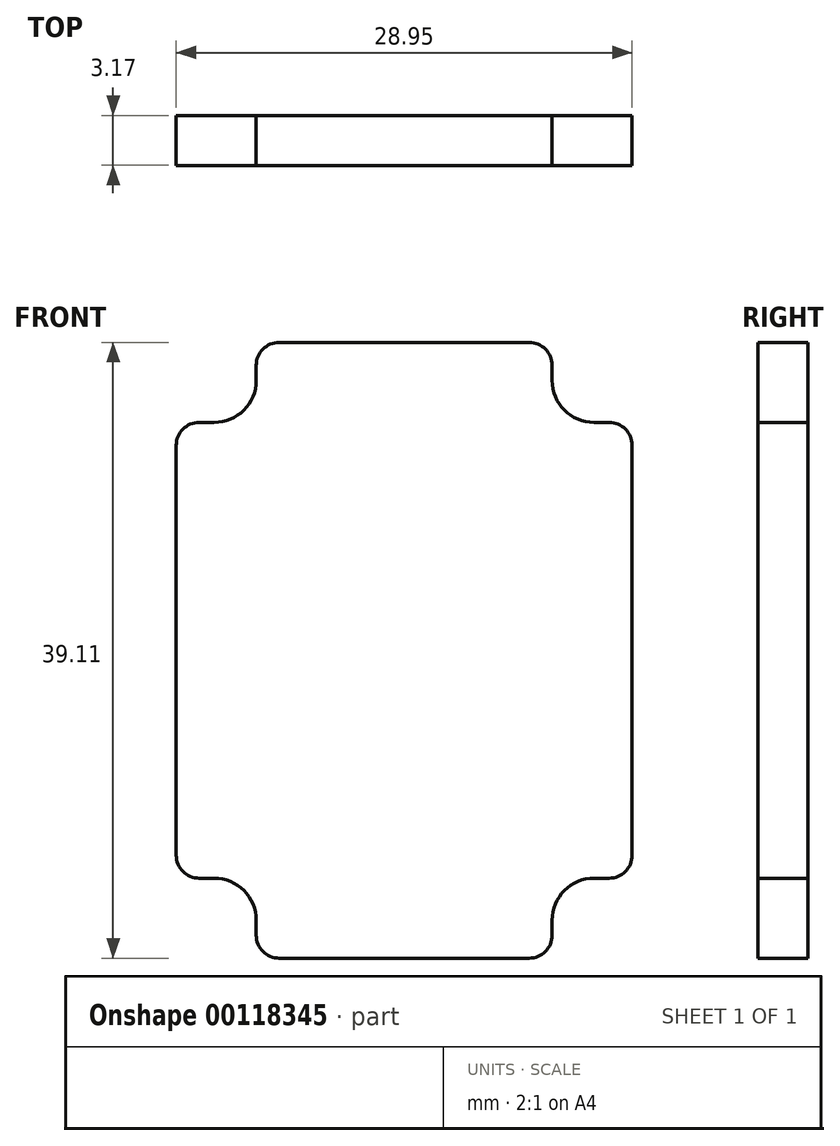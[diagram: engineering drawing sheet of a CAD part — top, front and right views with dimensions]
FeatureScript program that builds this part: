
annotation { "Feature Type Name" : "Feature", "Feature Type Description" : "" }
export const myFeature = defineFeature(function(context is Context, id is Id, definition is map)
    precondition{}
    {
        {
            var Q0;
            Q0=qCreatedBy(makeId("Front.planeOp"),FACE);
            var sketch = newSketch(context, id + "F0", { "sketchPlane" : qUnion([Q0])});
            skArc(sketch, "E0.0", {"start": v(-12.72, 14.33) * mm, "mid": v(-13.75, 13.9) * mm, "end": v(-14.18, 12.87) * mm});
            skLineSegment(sketch, "E0.1", {"start": v(12.36, -14.62) * mm, "end": v(13.31, -14.62) * mm});
            skArc(sketch, "E0.2", {"start": v(12.36, -14.62) * mm, "mid": v(10.47, -15.4) * mm, "end": v(9.7, -17.3) * mm});
            skLineSegment(sketch, "E0.3", {"start": v(9.7, -17.3) * mm, "end": v(9.7, -18.24) * mm});
            skArc(sketch, "E0.4", {"start": v(8.23, -19.7) * mm, "mid": v(9.26, -19.28) * mm, "end": v(9.7, -18.24) * mm});
            skLineSegment(sketch, "E0.5", {"start": v(-7.64, -19.7) * mm, "end": v(8.23, -19.7) * mm});
            skArc(sketch, "E0.6", {"start": v(-9.1, -18.24) * mm, "mid": v(-8.67, -19.28) * mm, "end": v(-7.64, -19.7) * mm});
            skArc(sketch, "E0.7", {"start": v(-14.18, -13.16) * mm, "mid": v(-13.75, -14.2) * mm, "end": v(-12.72, -14.62) * mm});
            skLineSegment(sketch, "E0.8", {"start": v(-12.72, -14.62) * mm, "end": v(-11.77, -14.62) * mm});
            skArc(sketch, "E0.9", {"start": v(-9.1, -17.3) * mm, "mid": v(-9.88, -15.4) * mm, "end": v(-11.77, -14.62) * mm});
            skLineSegment(sketch, "E0.10", {"start": v(-9.1, -17.3) * mm, "end": v(-9.1, -18.24) * mm});
            skArc(sketch, "E0.11", {"start": v(13.31, -14.62) * mm, "mid": v(14.34, -14.2) * mm, "end": v(14.77, -13.16) * mm});
            skLineSegment(sketch, "E0.12", {"start": v(-14.18, 12.87) * mm, "end": v(-14.18, -13.16) * mm});
            skLineSegment(sketch, "E0.13", {"start": v(14.77, 12.87) * mm, "end": v(14.77, -13.16) * mm});
            skArc(sketch, "E0.14", {"start": v(14.77, 12.87) * mm, "mid": v(14.34, 13.9) * mm, "end": v(13.31, 14.33) * mm});
            skLineSegment(sketch, "E0.15", {"start": v(12.36, 14.33) * mm, "end": v(13.31, 14.33) * mm});
            skArc(sketch, "E0.16", {"start": v(9.7, 17) * mm, "mid": v(10.47, 15.11) * mm, "end": v(12.36, 14.33) * mm});
            skLineSegment(sketch, "E0.17", {"start": v(9.7, 17.95) * mm, "end": v(9.7, 17) * mm});
            skArc(sketch, "E0.18", {"start": v(9.7, 17.95) * mm, "mid": v(9.26, 18.98) * mm, "end": v(8.23, 19.4) * mm});
            skLineSegment(sketch, "E0.19", {"start": v(-7.64, 19.4) * mm, "end": v(8.23, 19.4) * mm});
            skArc(sketch, "E0.20", {"start": v(-7.64, 19.4) * mm, "mid": v(-8.67, 18.98) * mm, "end": v(-9.1, 17.95) * mm});
            skLineSegment(sketch, "E0.21", {"start": v(-9.1, 17.95) * mm, "end": v(-9.1, 17) * mm});
            skArc(sketch, "E0.22", {"start": v(-11.77, 14.33) * mm, "mid": v(-9.88, 15.11) * mm, "end": v(-9.1, 17) * mm});
            skLineSegment(sketch, "E0.23", {"start": v(-12.72, 14.33) * mm, "end": v(-11.77, 14.33) * mm});
            skSolve(sketch);
        }
        {
            var Q0;
            Q0 = qSketchRegion(id + "F0", true);
            extrude(context, id + "F1", {"entities" : qUnion([Q0]), "depth" : 3.17 * mm});
        }
    });
